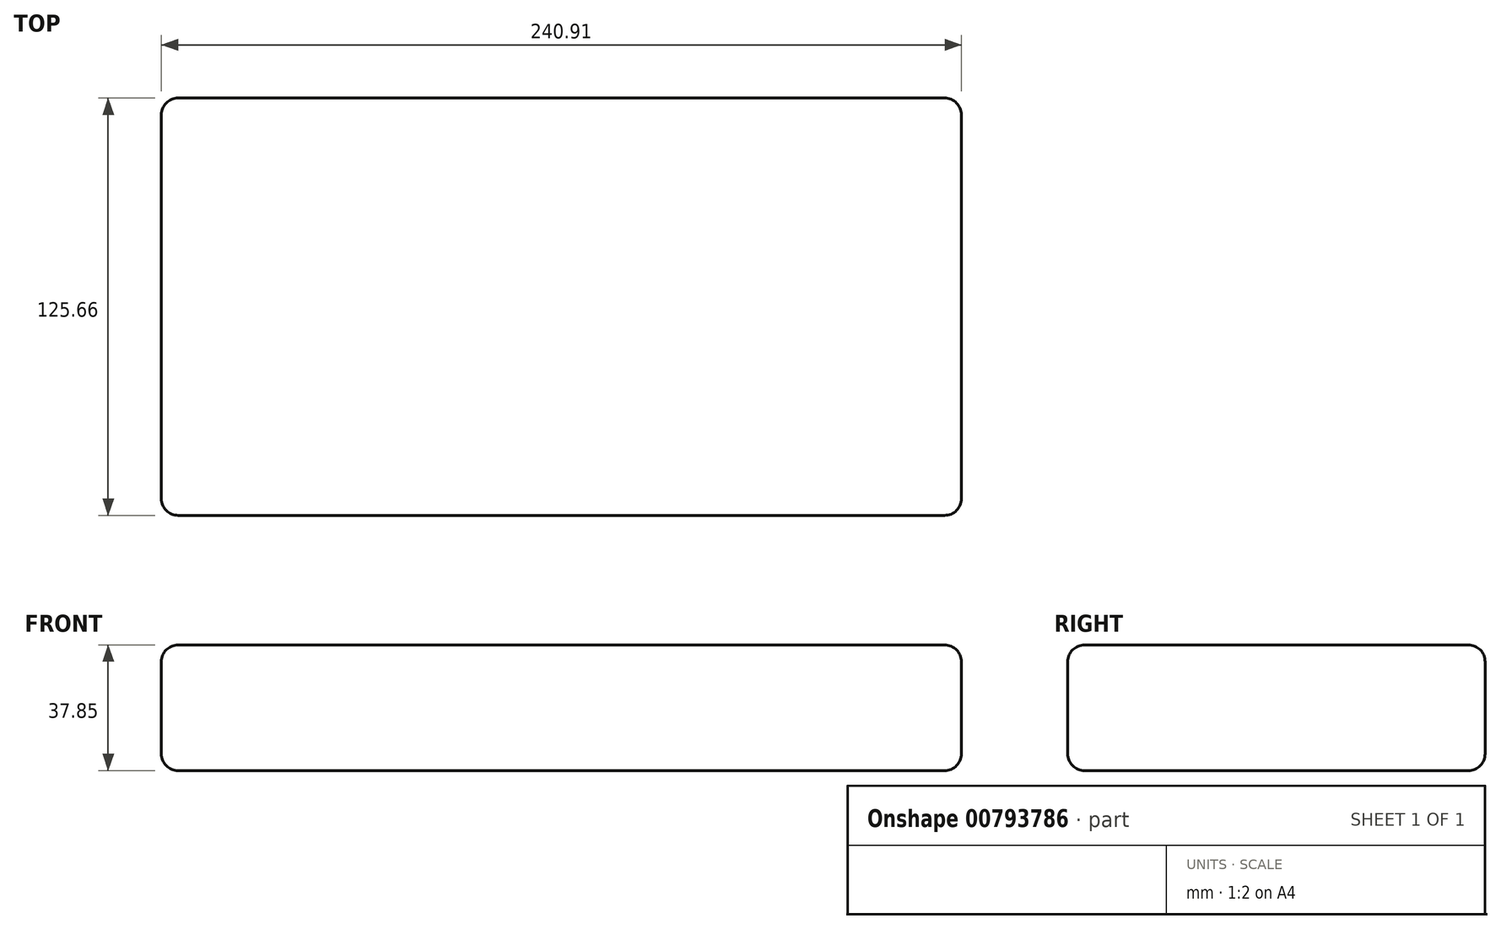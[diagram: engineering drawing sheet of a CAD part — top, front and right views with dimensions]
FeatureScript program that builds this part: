
annotation { "Feature Type Name" : "Feature", "Feature Type Description" : "" }
export const myFeature = defineFeature(function(context is Context, id is Id, definition is map)
    precondition{}
    {
        {
            var Q0;
            Q0=qCreatedBy(makeId("Top.planeOp"),FACE);
            var sketch = newSketch(context, id + "F0", { "sketchPlane" : qUnion([Q0])});
            skLineSegment(sketch, "E0.bottom", {"start": v(-117.04, 61.88) * mm, "end": v(123.87, 61.88) * mm});
            skLineSegment(sketch, "E0.top", {"start": v(-117.04, -63.78) * mm, "end": v(123.87, -63.78) * mm});
            skLineSegment(sketch, "E0.left", {"start": v(-117.04, 61.88) * mm, "end": v(-117.04, -63.78) * mm});
            skLineSegment(sketch, "E0.right", {"start": v(123.87, 61.88) * mm, "end": v(123.87, -63.78) * mm});
            skSolve(sketch);
        }
        {
            var Q0;
            Q0=makeQuery(id+"F0.imprint","IMPRINT",FACE,{"disambiguationData":[TD([[makeQuery(id+"F0.imprint","IMPRINT",EDGE,{"derivedFrom":sQuery(id+"F0.wireOp",EDGE,"E0.bottom")}),-1.0]])]});
            extrude(context, id + "F1", {"entities" : qUnion([Q0]), "depth" : 37.85 * mm, "offsetDistance" : 25.4 * mm});
        }
        {
            var Q0;
            Q0=makeQuery(id+"F1.opExtrude","CAP_FACE",FACE,{"disambiguationData":[OSD([sQuery(id+"F0.wireOp",EDGE,"E0.bottom"),sQuery(id+"F0.wireOp",EDGE,"E0.top"),sQuery(id+"F0.wireOp",EDGE,"E0.left"),sQuery(id+"F0.wireOp",EDGE,"E0.right")])],"isStart":false});
            var Q1;
            Q1=makeQuery(id+"F1.opExtrude","SWEPT_FACE",FACE,{"disambiguationData":[OSD([sQuery(id+"F0.wireOp",EDGE,"E0.right")])]});
            var Q2;
            Q2=makeQuery(id+"F1.opExtrude","CAP_EDGE",EDGE,{"disambiguationData":[OSD([sQuery(id+"F0.wireOp",EDGE,"E0.top")])],"isStart":true});
            var Q3;
            Q3=makeQuery(id+"F1.opExtrude","CAP_EDGE",EDGE,{"disambiguationData":[OSD([sQuery(id+"F0.wireOp",EDGE,"E0.bottom")])],"isStart":true});
            var Q4;
            Q4=makeQuery(id+"F1.opExtrude","SWEPT_EDGE",EDGE,{"disambiguationData":[OSD([sQuery(id+"F0.wireOp",EDGE,"E0.bottom"),sQuery(id+"F0.wireOp",EDGE,"E0.left")])]});
            var Q5;
            Q5=makeQuery(id+"F1.opExtrude","SWEPT_EDGE",EDGE,{"disambiguationData":[OSD([sQuery(id+"F0.wireOp",EDGE,"E0.top"),sQuery(id+"F0.wireOp",EDGE,"E0.left")])]});
            var Q6;
            Q6=makeQuery(id+"F1.opExtrude","CAP_EDGE",EDGE,{"disambiguationData":[OSD([sQuery(id+"F0.wireOp",EDGE,"E0.left")])],"isStart":true});
            var Q7;
            Q7=makeQuery(id+"F1.opExtrude","CAP_EDGE",EDGE,{"disambiguationData":[OSD([sQuery(id+"F0.wireOp",EDGE,"E0.right")])],"isStart":false});
            fillet(context, id + "F2", {"entities" : qUnion([Q0, Q1, Q2, Q3, Q4, Q5, Q6, Q7]), "radius" : 5.08 * mm, "tangentPropagation" : true, "allowEdgeOverflow" : false});
        }
    });
